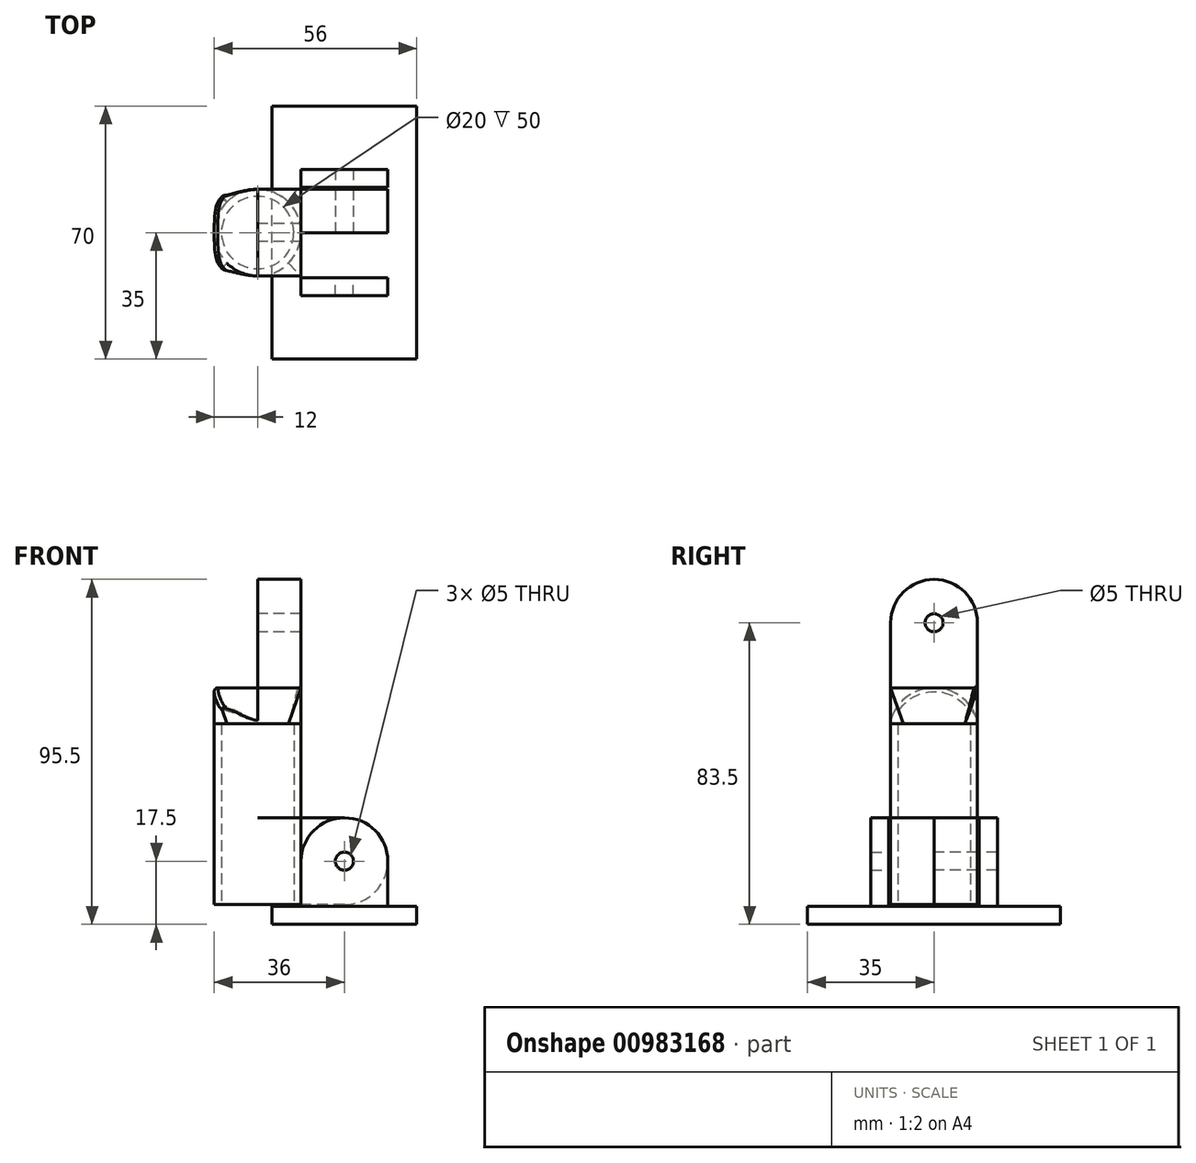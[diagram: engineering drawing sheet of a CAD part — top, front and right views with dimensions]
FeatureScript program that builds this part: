
annotation { "Feature Type Name" : "Feature", "Feature Type Description" : "" }
export const myFeature = defineFeature(function(context is Context, id is Id, definition is map)
    precondition{}
    {
        {
            var Q0;
            Q0=qCreatedBy(makeId("Top.planeOp"),FACE);
            var sketch = newSketch(context, id + "F0", { "sketchPlane" : qUnion([Q0])});
            skCircle(sketch, "E0", {"center": v(0, 0) * mm, "radius": 10 * mm});
            skCircle(sketch, "E1", {"center": v(0, 0) * mm, "radius": 12 * mm});
            skLineSegment(sketch, "E2", {"start": v(0, -12) * mm, "end": v(12, -12) * mm});
            skLineSegment(sketch, "E3", {"start": v(12, -12) * mm, "end": v(12, 12) * mm});
            skLineSegment(sketch, "E4", {"start": v(12, 12) * mm, "end": v(0, 12) * mm});
            skSolve(sketch);
        }
        {
            var Q0;
            Q0=makeQuery(id+"F0.imprint","IMPRINT",FACE,{"disambiguationData":[TD([[makeQuery(id+"F0.imprint","IMPRINT",EDGE,{"derivedFrom":sQuery(id+"F0.wireOp",EDGE,"E0")}),-1.0]])]});
            extrude(context, id + "F1", {"entities" : qUnion([Q0]), "depth" : 50 * mm, "offsetDistance" : 25 * mm});
        }
        {
            var Q0;
            Q0=makeQuery(id+"F1.opExtrude","CAP_FACE",FACE,{"disambiguationData":[OSD([sQuery(id+"F0.wireOp",EDGE,"E0"),sQuery(id+"F0.wireOp",EDGE,"E1")])],"isStart":false});
            var sketch = newSketch(context, id + "F2", { "sketchPlane" : qUnion([Q0])});
            skCircle(sketch, "E5.0", {"center": v(0, 0) * mm, "radius": 12 * mm});
            skSolve(sketch);
        }
        {
            var Q0;
            Q0=makeQuery(id+"F2.imprint","IMPRINT",FACE,{"disambiguationData":[TD([[makeQuery(id+"F2.imprint","IMPRINT",EDGE,{"derivedFrom":sQuery(id+"F2.wireOp",EDGE,"E5.0")}),1.0]])]});
            cPlane(context, id + "F3", {"entities" : qUnion([Q0]), "cplaneType" : CPlaneType.OFFSET, "offset" : 10 * mm, "width" : 150 * mm, "height" : 150 * mm});
        }
        {
            var Q0;
            Q0=qCreatedBy(id+"F3.planeOp",FACE);
            var sketch = newSketch(context, id + "F4", { "sketchPlane" : qUnion([Q0])});
            skLineSegment(sketch, "E6.bottom", {"start": v(-12, 12) * mm, "end": v(12, 12) * mm});
            skLineSegment(sketch, "E6.top", {"start": v(-12, -12) * mm, "end": v(12, -12) * mm});
            skLineSegment(sketch, "E6.left", {"start": v(-12, 12) * mm, "end": v(-12, -12) * mm});
            skLineSegment(sketch, "E6.right", {"start": v(12, 12) * mm, "end": v(12, -12) * mm});
            skPoint(sketch, "E6.middle", {"position": v(0, 0) * mm});
            skSolve(sketch);
        }
        {
            var Q1;
            Q1 = qSketchRegion(id + "F2", true);
            var Q2;
            Q2 = qSketchRegion(id + "F4", true);
            loft(context, id + "F5", {"operationType" : NewBodyOperationType.ADD, "sheetProfilesArray" : [{ "sheetProfileEntities" : qUnion([Q1]) }, { "sheetProfileEntities" : qUnion([Q2]) }]});
        }
        {
            var Q0;
            Q0=qCreatedBy(makeId("Right.planeOp"),FACE);
            var sketch = newSketch(context, id + "F6", { "sketchPlane" : qUnion([Q0])});
            skCircle(sketch, "E7", {"center": v(0, 78) * mm, "radius": 2.5 * mm});
            skArc(sketch, "E8", {"start": v(12, 78) * mm, "mid": v(0, 90) * mm, "end": v(-12, 78) * mm});
            skLineSegment(sketch, "E9", {"start": v(-12, 78) * mm, "end": v(-12, 60) * mm});
            skLineSegment(sketch, "E10", {"start": v(12, 78) * mm, "end": v(12, 60) * mm});
            skLineSegment(sketch, "E11", {"start": v(-12, 60) * mm, "end": v(12, 60) * mm});
            skSolve(sketch);
        }
        {
            var Q0;
            Q0 = qSketchRegion(id + "F6", true);
            var Q1;
            Q1=makeQuery(id+"F5.opLoft","MID_CAP_VERTEX",VERTEX,{"disambiguationData":[OSD([sQuery(id+"F4.wireOp",EDGE,"E6.bottom"),sQuery(id+"F4.wireOp",EDGE,"E6.right")])],"capPos":1.0});
            extrude(context, id + "F7", {"entities" : qUnion([Q0]), "operationType" : NewBodyOperationType.ADD, "endBound" : BoundingType.UP_TO_VERTEX, "depth" : 25 * mm, "endBoundEntityVertex" : qUnion([Q1]), "offsetDistance" : 25 * mm});
        }
        {
            var Q0;
            Q0=makeQuery(id+"F7.opExtrude","CAP_FACE",FACE,{"disambiguationData":[OSD([sQuery(id+"F6.wireOp",EDGE,"E7"),sQuery(id+"F6.wireOp",EDGE,"E8"),sQuery(id+"F6.wireOp",EDGE,"E9"),sQuery(id+"F6.wireOp",EDGE,"E10"),sQuery(id+"F6.wireOp",EDGE,"E11")])],"isStart":true});
            var sketch = newSketch(context, id + "F8", { "sketchPlane" : qUnion([Q0])});
            skCircle(sketch, "E12", {"center": v(0, 78) * mm, "radius": 12 * mm, "construction": true});
            skPoint(sketch, "E13", {"position": v(0, 66) * mm});
            skPoint(sketch, "E14", {"position": v(0, 60) * mm});
            skArc(sketch, "E15", {"start": v(-12, 51) * mm, "mid": v(0, 60) * mm, "end": v(12, 51) * mm});
            skLineSegment(sketch, "E16", {"start": v(-12, 51) * mm, "end": v(-12, 60) * mm});
            skLineSegment(sketch, "E17", {"start": v(-12, 60) * mm, "end": v(12, 60) * mm});
            skLineSegment(sketch, "E18", {"start": v(12, 60) * mm, "end": v(12, 51) * mm});
            skSolve(sketch);
        }
        {
            var Q0;
            Q0 = qSketchRegion(id + "F8", true);
            extrude(context, id + "F9", {"entities" : qUnion([Q0]), "operationType" : NewBodyOperationType.REMOVE, "endBound" : BoundingType.THROUGH_ALL, "depth" : 25 * mm, "offsetDistance" : 25 * mm});
        }
        {
            var Q0;
            {var subQ0=sQuery(id+"F4.wireOp",EDGE,"E6.top");var subQ1=sQuery(id+"F4.wireOp",EDGE,"E6.right");var subQ2=sQuery(id+"F4.wireOp",EDGE,"E6.left");var subQ3=sQuery(id+"F4.wireOp",EDGE,"E6.bottom");var subQ4=sQuery(id+"F2.wireOp",EDGE,"E5.0");Q0=makeQuery(id+"F9.boolean.opBoolean","INTERSECT",EDGE,{"derivedFrom":[makeQuery(id+"F5.opLoft","SWEPT_FACE",FACE,{"disambiguationData":[OSD([subQ4,subQ3,subQ0,subQ2,subQ1]),TDD([makeQuery(id+"F2.imprint","IMPRINT",EDGE,{"derivedFrom":subQ4}),makeQuery(id+"F4.imprint","INTERSECT",VERTEX,{"derivedFrom":[subQ3,subQ2]}),makeQuery(id+"F4.imprint","INTERSECT",VERTEX,{"derivedFrom":[subQ0,subQ2]}),makeQuery(id+"F4.imprint","INTERSECT",VERTEX,{"derivedFrom":[subQ0,subQ1]}),makeQuery(id+"F4.imprint","IMPRINT",EDGE,{"derivedFrom":subQ0})])]}),makeQuery(id+"F9.opExtrude","SWEPT_FACE",FACE,{"disambiguationData":[OSD([sQuery(id+"F8.wireOp",EDGE,"E15")])]})]});}
            var Q1;
            Q1=makeQuery(id+"F9.boolean.opBoolean","INTERSECT",EDGE,{"derivedFrom":[makeQuery(id+"F5.opLoft","SWEPT_FACE",FACE,{"disambiguationData":[OSD([sQuery(id+"F2.wireOp",EDGE,"E5.0"),sQuery(id+"F4.wireOp",EDGE,"E6.bottom"),sQuery(id+"F4.wireOp",EDGE,"E6.top"),sQuery(id+"F4.wireOp",EDGE,"E6.left")])]}),makeQuery(id+"F9.opExtrude","SWEPT_FACE",FACE,{"disambiguationData":[OSD([sQuery(id+"F8.wireOp",EDGE,"E15")])]})]});
            var Q2;
            {var subQ0=sQuery(id+"F4.wireOp",EDGE,"E6.bottom");var subQ1=sQuery(id+"F4.wireOp",EDGE,"E6.right");var subQ2=sQuery(id+"F4.wireOp",EDGE,"E6.top");var subQ3=sQuery(id+"F4.wireOp",EDGE,"E6.left");var subQ4=sQuery(id+"F2.wireOp",EDGE,"E5.0");Q2=makeQuery(id+"F9.boolean.opBoolean","INTERSECT",EDGE,{"derivedFrom":[makeQuery(id+"F5.opLoft","SWEPT_FACE",FACE,{"disambiguationData":[OSD([subQ4,subQ0,subQ2,subQ3,subQ1]),TDD([makeQuery(id+"F2.imprint","IMPRINT",EDGE,{"derivedFrom":subQ4}),makeQuery(id+"F4.imprint","INTERSECT",VERTEX,{"derivedFrom":[subQ0,subQ3]}),makeQuery(id+"F4.imprint","INTERSECT",VERTEX,{"derivedFrom":[subQ0,subQ1]}),makeQuery(id+"F4.imprint","INTERSECT",VERTEX,{"derivedFrom":[subQ2,subQ1]}),makeQuery(id+"F4.imprint","IMPRINT",EDGE,{"derivedFrom":subQ0})])]}),makeQuery(id+"F9.opExtrude","SWEPT_FACE",FACE,{"disambiguationData":[OSD([sQuery(id+"F8.wireOp",EDGE,"E15")])]})]});}
            var Q3;
            Q3=makeQuery(id+"F5.opLoft","SWEPT_EDGE",EDGE,{"disambiguationData":[OSD([sQuery(id+"F2.wireOp",EDGE,"E5.0"),sQuery(id+"F4.wireOp",EDGE,"E6.bottom"),sQuery(id+"F4.wireOp",EDGE,"E6.top"),sQuery(id+"F4.wireOp",EDGE,"E6.left")])]});
            var Q4;
            Q4=makeQuery(id+"F5.opLoft","SWEPT_EDGE",EDGE,{"disambiguationData":[OSD([sQuery(id+"F4.wireOp",EDGE,"E6.bottom"),sQuery(id+"F4.wireOp",EDGE,"E6.left")])]});
            fillet(context, id + "F10", {"entities" : qUnion([Q0, Q1, Q2, Q3, Q4]), "radius" : 1 * mm, "tangentPropagation" : true, "allowEdgeOverflow" : false});
        }
        {
            var Q0;
            Q0 = qSketchRegion(id + "F0", true);
            extrude(context, id + "F11", {"entities" : qUnion([Q0]), "depth" : 24 * mm, "offsetDistance" : 25 * mm});
        }
        {
            var Q0;
            Q0=qCreatedBy(makeId("Front.planeOp"),FACE);
            var sketch = newSketch(context, id + "F12", { "sketchPlane" : qUnion([Q0])});
            skLineSegment(sketch, "E19.0", {"start": v(12, 24) * mm, "end": v(12, 0) * mm});
            skCircle(sketch, "E20", {"center": v(24, 12) * mm, "radius": 2.5 * mm});
            skPoint(sketch, "E20.centerSnap0", {"position": v(12, 12) * mm});
            skArc(sketch, "E21", {"start": v(24, 24) * mm, "mid": v(36, 12) * mm, "end": v(24, 0) * mm});
            skLineSegment(sketch, "E22", {"start": v(24, 24) * mm, "end": v(12, 24) * mm});
            skLineSegment(sketch, "E23", {"start": v(24, 0) * mm, "end": v(12, 0) * mm});
            skSolve(sketch);
        }
        {
            var Q0;
            Q0=makeQuery(id+"F12.imprint","IMPRINT",FACE,{"disambiguationData":[TD([[makeQuery(id+"F12.imprint","IMPRINT",EDGE,{"derivedFrom":sQuery(id+"F12.wireOp",EDGE,"E19.0")}),1.0]])]});
            var Q1;
            Q1=makeQuery(id+"F11.opExtrude","SWEPT_FACE",FACE,{"disambiguationData":[OSD([sQuery(id+"F0.wireOp",EDGE,"E4")])]});
            extrude(context, id + "F13", {"entities" : qUnion([Q0]), "operationType" : NewBodyOperationType.ADD, "endBound" : BoundingType.UP_TO_SURFACE, "oppositeDirection" : true, "depth" : 25 * mm, "endBoundEntityFace" : qUnion([Q1]), "offsetDistance" : 25 * mm});
        }
        {
            var Q0;
            Q0=makeQuery(id+"F13.boolean.opBoolean","MERGE",FACE,{"derivedFrom":[makeQuery(id+"F11.opExtrude","SWEPT_FACE",FACE,{"disambiguationData":[OSD([sQuery(id+"F0.wireOp",EDGE,"E4")])]}),makeQuery(id+"F13.opExtrude","CAP_FACE",FACE,{"disambiguationData":[OSD([sQuery(id+"F12.wireOp",EDGE,"E19.0"),sQuery(id+"F12.wireOp",EDGE,"E20"),sQuery(id+"F12.wireOp",EDGE,"E21"),sQuery(id+"F12.wireOp",EDGE,"E22"),sQuery(id+"F12.wireOp",EDGE,"E23")])],"isStart":false})]});
            cPlane(context, id + "F14", {"entities" : qUnion([Q0]), "cplaneType" : CPlaneType.OFFSET, "offset" : 0.5 * mm, "width" : 150 * mm, "height" : 150 * mm});
        }
        {
            var Q0;
            Q0=qCreatedBy(id+"F14.planeOp",FACE);
            var sketch = newSketch(context, id + "F15", { "sketchPlane" : qUnion([Q0])});
            skArc(sketch, "E24", {"start": v(-36, 12) * mm, "mid": v(-24, 24) * mm, "end": v(-12, 12) * mm});
            skLineSegment(sketch, "E25", {"start": v(-36, 12) * mm, "end": v(-36, -0.5) * mm});
            skLineSegment(sketch, "E26", {"start": v(-36, -0.5) * mm, "end": v(-12, -0.5) * mm});
            skLineSegment(sketch, "E27", {"start": v(-12, -0.5) * mm, "end": v(-12, 12) * mm});
            skCircle(sketch, "E28", {"center": v(-24, 12) * mm, "radius": 2.5 * mm});
            skSolve(sketch);
        }
        {
            var Q0;
            {var subQ6=sQuery(id+"F15.wireOp",EDGE,"E25");Q0=makeQuery(id+"F15.imprint","IMPRINT",FACE,{"disambiguationData":[TD([[makeQuery(id+"F15.imprint","IMPRINT",EDGE,{"derivedFrom":subQ6}),1.0]])]});}
            var Q1;
            Q1=makeQuery(id+"F15.imprint","IMPRINT",FACE,{"disambiguationData":[TD([[makeQuery(id+"F15.imprint","IMPRINT",EDGE,{"derivedFrom":makeQuery(id+"F13.opExtrude","CAP_EDGE",EDGE,{"disambiguationData":[OSD([sQuery(id+"F12.wireOp",EDGE,"E20")])],"isStart":false})}),-1.0]])]});
            extrude(context, id + "F16", {"entities" : qUnion([Q0, Q1]), "depth" : 5 * mm, "offsetDistance" : 25 * mm});
        }
        {
            var Q0;
            Q0=makeQuery(id+"F16.opExtrude","SWEPT_BODY",BODY,{"disambiguationData":[OSD([sQuery(id+"F15.wireOp",EDGE,"E24"),sQuery(id+"F15.wireOp",EDGE,"E25"),sQuery(id+"F15.wireOp",EDGE,"E26"),sQuery(id+"F15.wireOp",EDGE,"E27"),sQuery(id+"F15.wireOp",EDGE,"E28")])]});
            var Q1;
            Q1=qCreatedBy(makeId("Front.planeOp"),FACE);
            mirror(context, id + "F17", {"entities" : qUnion([Q0]), "mirrorPlane" : qUnion([Q1])});
        }
        {
            var Q0;
            Q0=makeQuery(id+"F16.opExtrude","SWEPT_FACE",FACE,{"disambiguationData":[OSD([sQuery(id+"F15.wireOp",EDGE,"E26")])]});
            var sketch = newSketch(context, id + "F18", { "sketchPlane" : qUnion([Q0])});
            skLineSegment(sketch, "E29.bottom", {"start": v(44, 35) * mm, "end": v(4, 35) * mm});
            skLineSegment(sketch, "E29.top", {"start": v(44, -35) * mm, "end": v(4, -35) * mm});
            skLineSegment(sketch, "E29.left", {"start": v(44, 35) * mm, "end": v(44, -35) * mm});
            skLineSegment(sketch, "E29.right", {"start": v(4, 35) * mm, "end": v(4, -35) * mm});
            skPoint(sketch, "E29.middle", {"position": v(24, 0) * mm});
            skSolve(sketch);
        }
        {
            var Q0;
            Q0=makeQuery(id+"F18.imprint","IMPRINT",FACE,{"disambiguationData":[TD([[makeQuery(id+"F18.imprint","IMPRINT",EDGE,{"derivedFrom":sQuery(id+"F18.wireOp",EDGE,"E29.bottom")}),1.0]])]});
            var Q1;
            {var subQ0=sQuery(id+"F15.wireOp",EDGE,"E26");Q1=makeQuery(id+"F18.imprint","IMPRINT",FACE,{"disambiguationData":[TD([[makeQuery(id+"F18.imprint","IMPRINT",EDGE,{"derivedFrom":makeQuery(id+"F16.opExtrude","CAP_EDGE",EDGE,{"disambiguationData":[OSD([subQ0])],"isStart":true})}),1.0]])]});}
            extrude(context, id + "F19", {"entities" : qUnion([Q0, Q1]), "operationType" : NewBodyOperationType.ADD, "depth" : 5 * mm, "offsetDistance" : 25 * mm});
        }
    });
